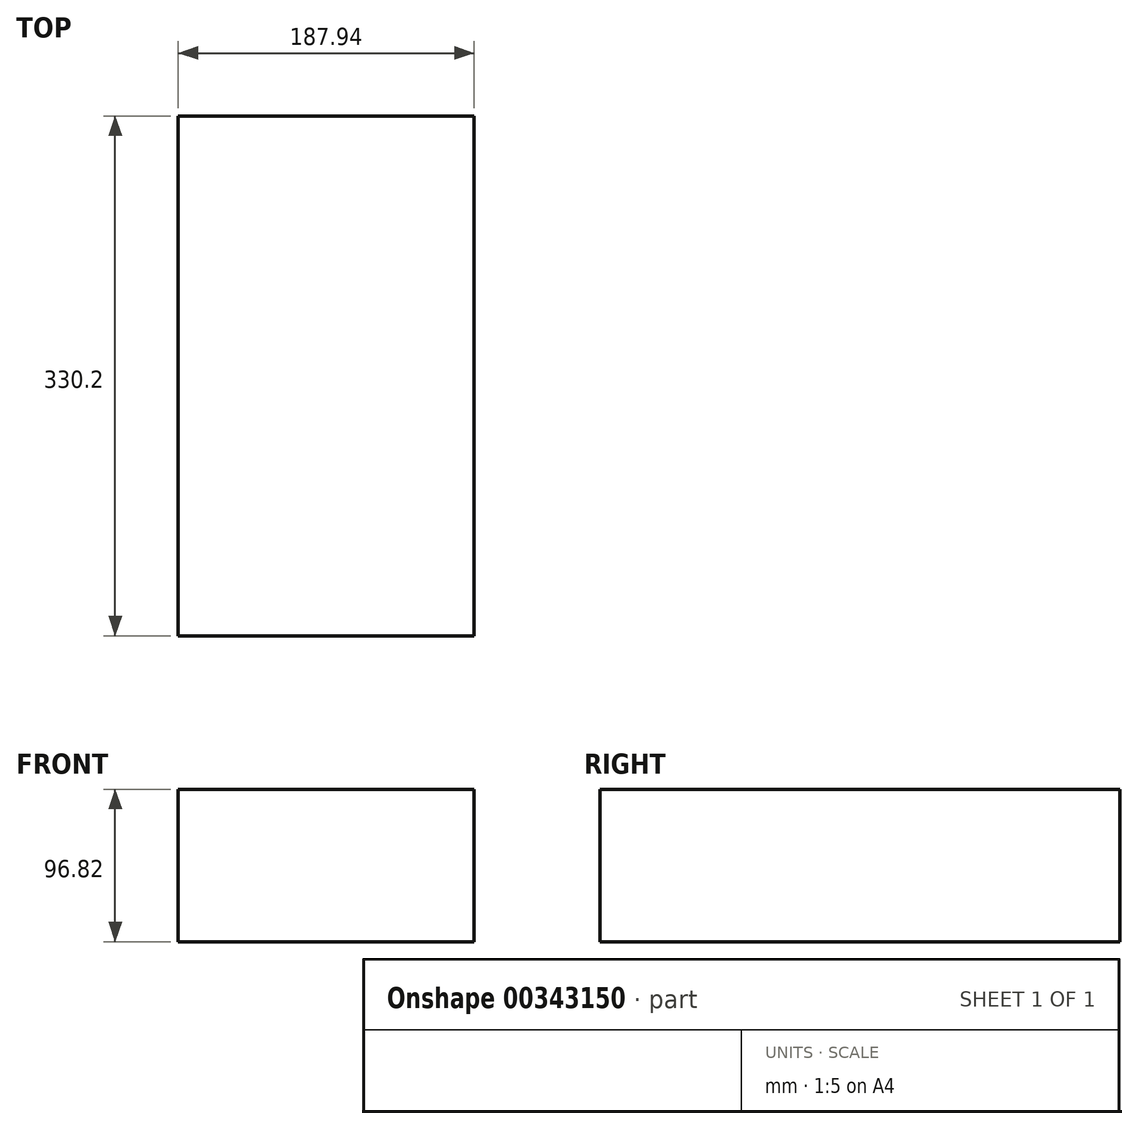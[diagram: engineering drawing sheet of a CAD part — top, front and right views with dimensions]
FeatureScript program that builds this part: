
annotation { "Feature Type Name" : "Feature", "Feature Type Description" : "" }
export const myFeature = defineFeature(function(context is Context, id is Id, definition is map)
    precondition{}
    {
        {
            var Q0;
            Q0=qCreatedBy(makeId("Front.planeOp"),FACE);
            var sketch = newSketch(context, id + "F0", { "sketchPlane" : qUnion([Q0])});
            skLineSegment(sketch, "E0.bottom", {"start": v(93.97, -48.41) * mm, "end": v(-93.97, -48.41) * mm});
            skLineSegment(sketch, "E0.top", {"start": v(93.97, 48.41) * mm, "end": v(-93.97, 48.41) * mm});
            skLineSegment(sketch, "E0.left", {"start": v(93.97, -48.41) * mm, "end": v(93.97, 48.41) * mm});
            skLineSegment(sketch, "E0.right", {"start": v(-93.97, -48.41) * mm, "end": v(-93.97, 48.41) * mm});
            skPoint(sketch, "E0.middle", {"position": v(0, 0) * mm});
            skSolve(sketch);
        }
        {
            var Q0;
            Q0=makeQuery(id+"F0.imprint","IMPRINT",FACE,{"disambiguationData":[TD([[makeQuery(id+"F0.imprint","IMPRINT",EDGE,{"derivedFrom":sQuery(id+"F0.wireOp",EDGE,"E0.bottom")}),-1.0]])]});
            extrude(context, id + "F1", {"entities" : qUnion([Q0]), "depth" : 330.2 * mm});
        }
    });
